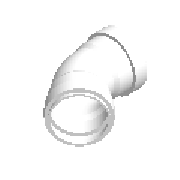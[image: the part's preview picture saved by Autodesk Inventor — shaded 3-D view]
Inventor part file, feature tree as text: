
AUTODESK INVENTOR PART (.ipt)
format: ipt  version: 2023.1 (Build 271208000, 208)  size: 279,552 bytes
history: native  units: mm (DEFAULTED — no unit token found)
features: other x4, sketch x3, revolve x1
ambient origin geometry x8: Origin, YZ Plane, XZ Plane, XY Plane, X Axis, Y Axis, Z Axis, Center Point
bodies: Solid1 (feature_tree)
feature tree (8):
  sketch  "Sketch1"  dims[d3=90.0deg d0=2.4mm]
  revolve  "Revolution1"  [1 undecoded]
  sketch  "Sketch2"  dims[d1=2.4mm]
  other  "Work Axis31"
  other  "Work Point21"
  other  "Work Axis32"
  other  "Work Point22"
  sketch  "Sketch3"  dims[d2=2.4mm d4=2.88mm d5=2.4mm d6=7.2mm d7=160.5mm d8=32.0mm d9=42.0mm d10=0.0mm d11=11.2mm d12=160.0mm d13=3.2mm d14=2.88mm d15=45.0deg d16=42.0mm d17=42.0mm d18=160.5mm d19=2.4mm d20=2.4mm d21=2.4mm d22=2.4mm d23=4.8mm d24=2.88mm d25=3.2mm d26=160.0mm d27=11.2mm d28=32.0mm d29=42.0mm d30=45.0deg d31=42.0mm d32=42.0mm d33=2.88mm d206=90.0deg d207=0.0mm]
note: 1 required parameter value undecoded (feature->parameter linkage not recoverable at this tier; creation-order binding heuristic only, values carry confidence <= 0.55)
